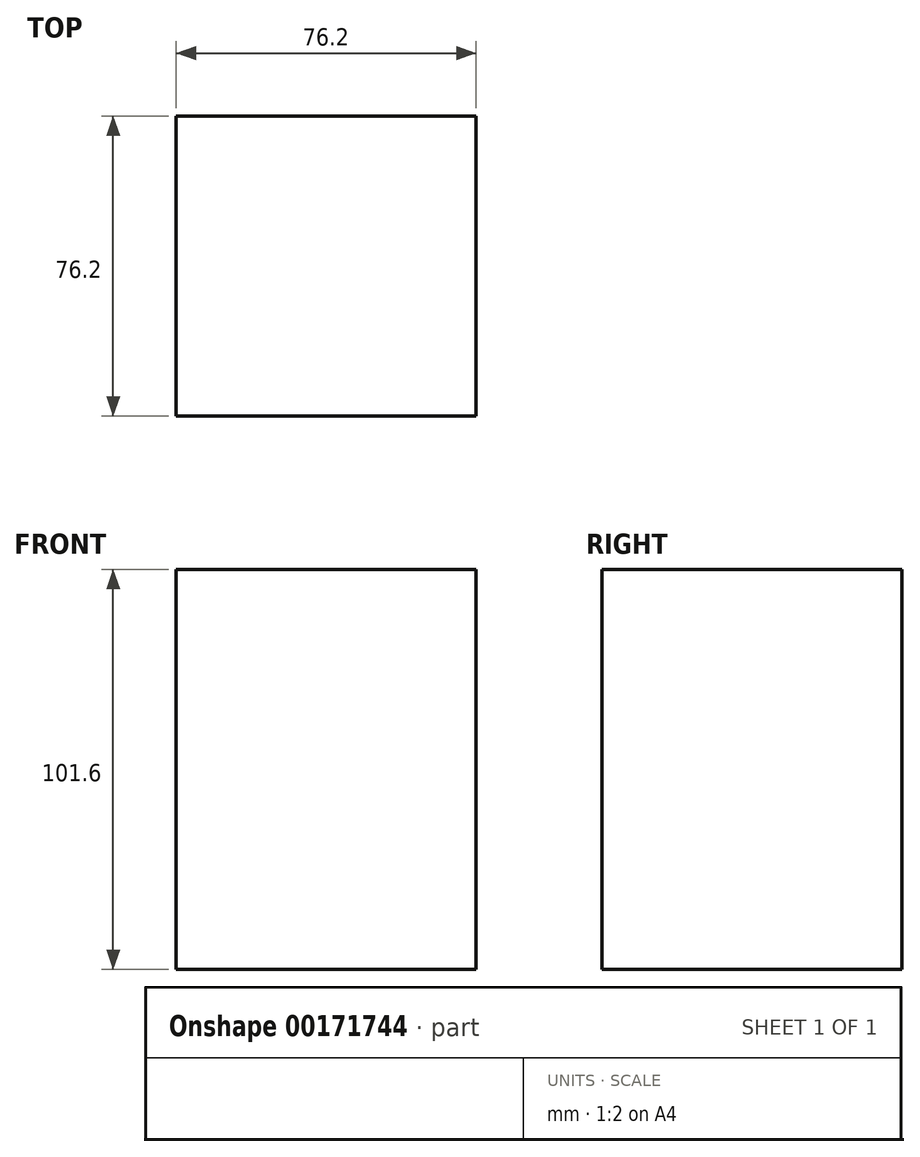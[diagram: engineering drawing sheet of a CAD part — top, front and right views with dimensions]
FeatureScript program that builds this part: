
annotation { "Feature Type Name" : "Feature", "Feature Type Description" : "" }
export const myFeature = defineFeature(function(context is Context, id is Id, definition is map)
    precondition{}
    {
        {
            var Q0;
            Q0=qCreatedBy(makeId("Top.planeOp"),FACE);
            var sketch = newSketch(context, id + "F0", { "sketchPlane" : qUnion([Q0])});
            skLineSegment(sketch, "E0.bottom", {"start": v(0, 0) * mm, "end": v(76.2, 0) * mm});
            skLineSegment(sketch, "E0.top", {"start": v(0, -76.2) * mm, "end": v(76.2, -76.2) * mm});
            skLineSegment(sketch, "E0.left", {"start": v(0, 0) * mm, "end": v(0, -76.2) * mm});
            skLineSegment(sketch, "E0.right", {"start": v(76.2, 0) * mm, "end": v(76.2, -76.2) * mm});
            skSolve(sketch);
        }
        {
            var Q0;
            Q0 = qSketchRegion(id + "F0", true);
            extrude(context, id + "F1", {"entities" : qUnion([Q0]), "depth" : 101.6 * mm});
        }
    });
